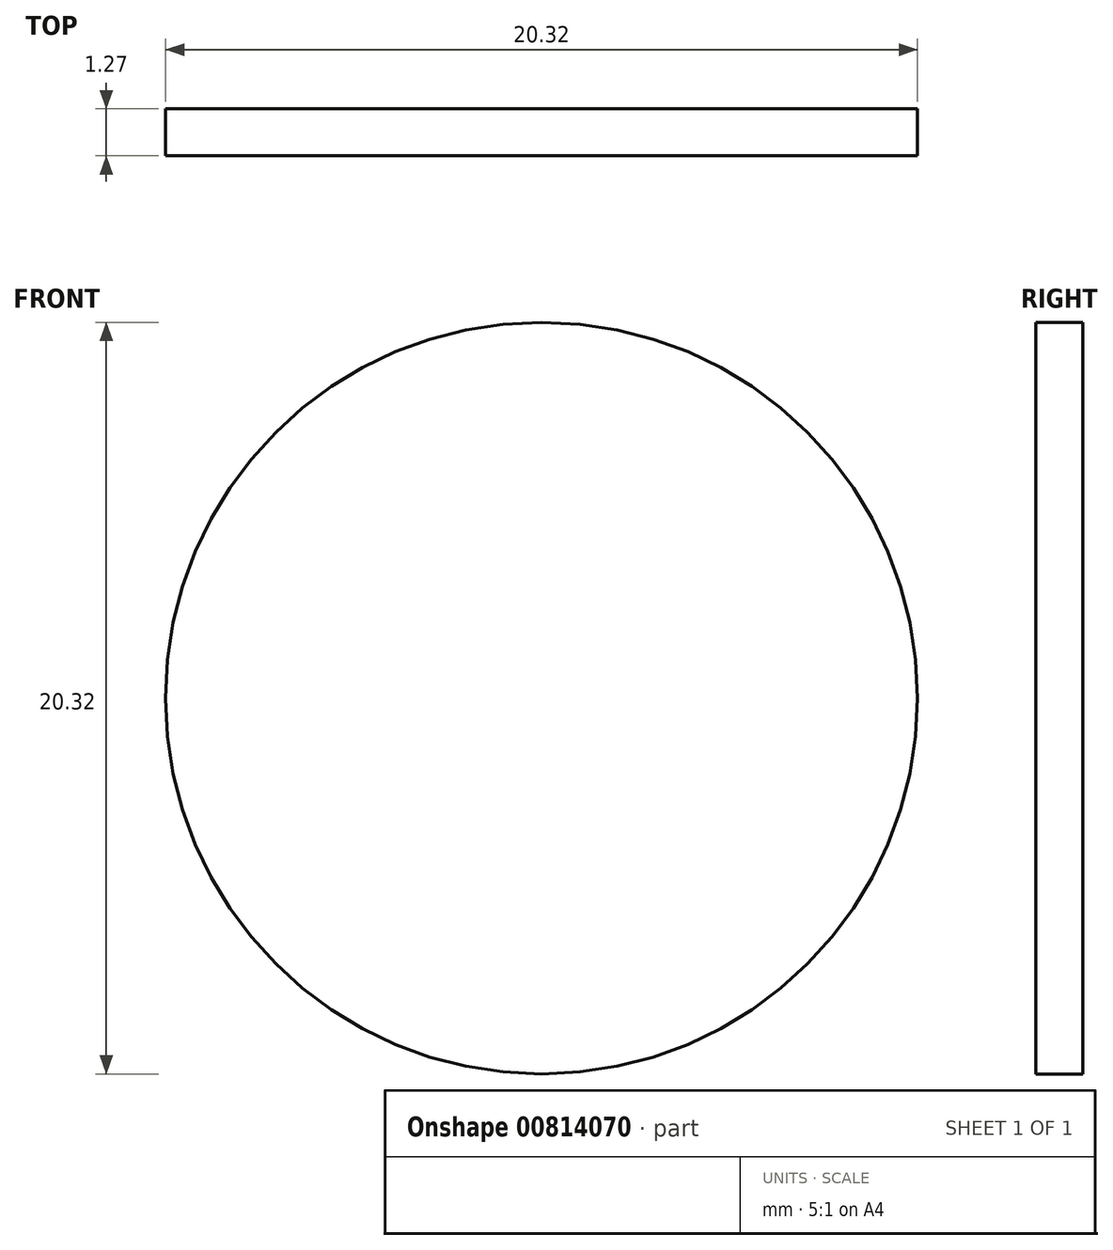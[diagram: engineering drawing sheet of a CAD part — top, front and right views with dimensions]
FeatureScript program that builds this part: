
annotation { "Feature Type Name" : "Feature", "Feature Type Description" : "" }
export const myFeature = defineFeature(function(context is Context, id is Id, definition is map)
    precondition{}
    {
        {
            var Q0;
            Q0=qCreatedBy(makeId("Front.planeOp"),FACE);
            var sketch = newSketch(context, id + "F0", { "sketchPlane" : qUnion([Q0])});
            skCircle(sketch, "E0", {"center": v(0, 0) * mm, "radius": 10.16 * mm});
            skSolve(sketch);
        }
        {
            var Q0;
            Q0 = qSketchRegion(id + "F0", true);
            extrude(context, id + "F1", {"entities" : qUnion([Q0]), "depth" : 1.27 * mm, "offsetDistance" : 25.4 * mm});
        }
    });
